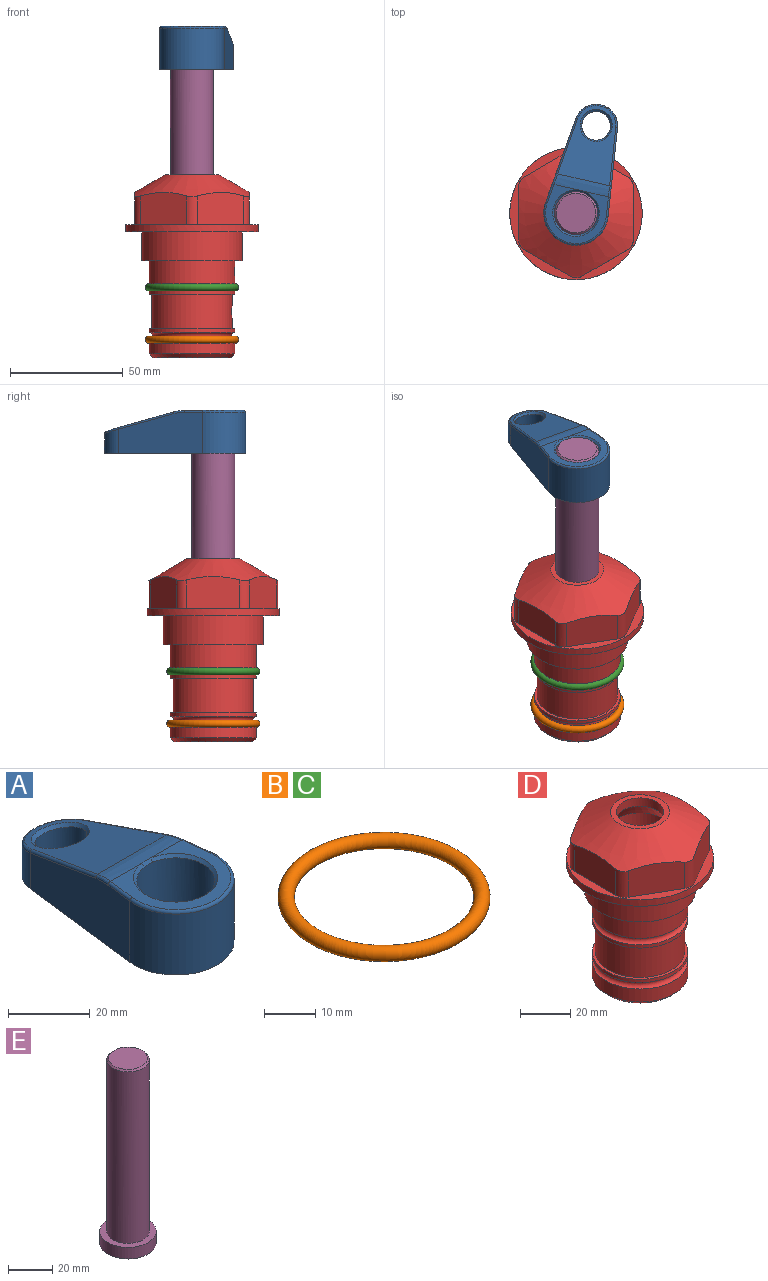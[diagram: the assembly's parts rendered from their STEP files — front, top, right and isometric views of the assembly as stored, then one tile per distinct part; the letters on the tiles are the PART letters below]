
ASSEMBLY  parts=5 mates=4
PART A: 31 faces, bbox 31.7x65.5x19.8 mm
  f0: plane 39.12x18.26mm, normal (0.99,0.12,0), area 612.2mm2, adj f1,f4,f7,f11,f13,f15
  f1: cylinder r=9.53mm len=18.91mm, axis (0,0,-1), area 296.1mm2, adj f0,f2,f7,f17
  f2: plane 39.12x18.26mm, normal (-0.99,0.12,0), area 612.2mm2, adj f1,f4,f7,f12,f14,f16
  f3: cylinder r=6.35mm len=12.7mm, axis (0,0,-1), area 362.4mm2, adj f7,f18
  f4: cylinder r=14.29mm len=28.58mm, axis (0,0,-1), area 882.2mm2, adj f0,f2,f7,f10
  f5: cylinder r=9.53mm len=19.05mm, axis (0,0,-1), area 1092.6mm2, adj f7,f19,f20
  f6: plane 26.99x23.69mm, normal (0,0,1), area 216.2mm2, adj f9,f10,f11,f12,f19
  f7: plane 63.5x28.58mm, normal (0,0,-1), area 661.8mm2, adj f0,f1,f2,f3,f4,f5,f22,f23
  f8: plane 33.52x23.6mm, normal (0,0.26,0.97), area 486mm2, adj f9,f15,f16,f17,f18
  f9: cylinder r=19.05mm len=24.72mm, axis (1,0,0), area 120.4mm2, adj f6,f8,f13,f14,f20
  f10: torus R=13.49mm, axis (0,0,1), area 59mm2, adj f4,f6,f11,f12
  f11: cylinder r=0.79mm len=8.67mm, axis (0.12,-0.99,0), area 10.8mm2, adj f0,f6,f10,f13
  f12: cylinder r=0.79mm len=8.67mm, axis (0.12,0.99,0), area 10.8mm2, adj f2,f6,f10,f14
  f13: bspline ~4.95x1.42mm, area 6.1mm2, adj f0,f9,f11,f15
  f14: bspline ~4.95x1.42mm, area 6.1mm2, adj f2,f9,f12,f16
  f15: cylinder r=0.79mm len=25.95mm, axis (0.12,-0.96,0.26), area 32.9mm2, adj f0,f8,f13,f17
  f16: cylinder r=0.79mm len=25.95mm, axis (0.12,0.96,-0.26), area 32.9mm2, adj f2,f8,f14,f17
  f17: bspline ~18.91x8.38mm, area 30mm2, adj f1,f8,f15,f16
  f18: bspline ~14.29x14.29mm, area 48.3mm2, adj f3,f8
  f19: cone r=9.53mm half-angle=45deg, axis (0,0,1), area 66.5mm2, adj f5,f6,f20
  f20: bspline ~3.22x0.96mm, area 3.5mm2, adj f5,f9,f19
  f21: plane 2.75x2.72mm, normal (0,0,-1), area 2.9mm2, adj f23,f25,f28
  f22: plane 23.05x15.88mm, normal (-0.99,-0.12,0), area 323.6mm2, adj f7,f25,f26,f27,f28,f29
  f23: plane 23.05x15.88mm, normal (0.99,-0.12,0), area 323.6mm2, adj f7,f21,f25,f27,f28,f30
  f24: cylinder r=9.53mm len=10.69mm, axis (0,0,-1), area 114.7mm2, adj f7,f27,f29,f30
  f25: cylinder r=12.7mm len=20.59mm, axis (0,0,-1), area 381.1mm2, adj f7,f21,f22,f23,f26,f28
  f26: plane 2.75x2.72mm, normal (0,0,-1), area 2.9mm2, adj f22,f25,f28
  f27: plane 19.72x18.37mm, normal (0,-0.26,-0.97), area 291.8mm2, adj f22,f23,f24,f28,f29,f30
  f28: cylinder r=15.88mm len=19.92mm, axis (1,0,0), area 54.8mm2, adj f21,f22,f23,f25,f26,f27
  f29: cylinder r=1.59mm len=11mm, axis (0,0,-1), area 34.7mm2, adj f7,f22,f24,f27
  f30: cylinder r=1.59mm len=11mm, axis (0,0,-1), area 34.7mm2, adj f7,f23,f24,f27
PART B: 1 faces, bbox 44.7x44.7x3.2 mm
  f0: torus R=19.05mm, axis (0,0,1), area 1193.9mm2
PART C: same geometry as B
PART D: 36 faces, bbox 58.7x58.7x81 mm
  f0: cylinder r=17.78mm len=35.56mm, axis (0,0,1), area 1670.8mm2, adj f23,f24,f31
  f1: cylinder r=19.05mm len=38.1mm, axis (0,0,1), area 1191.9mm2, adj f26,f27,f30
  f2: plane 58.66x58.66mm, normal (0,0,-1), area 1150.6mm2, adj f3,f28
  f3: cylinder r=29.33mm len=58.66mm, axis (0,0,-1), area 585.1mm2, adj f2,f4
  f4: plane 58.66x58.66mm, normal (0,0,1), area 475.9mm2, adj f3,f5,f6,f7,f8,f9,f10,f11
  f5: plane 20.32x14.34mm, normal (-0.5,0.87,0), area 324.4mm2, adj f4,f15,f16,f17
  f6: plane 20.32x14.34mm, normal (0.5,0.87,0), area 324.4mm2, adj f4,f14,f15,f17
  f7: plane 23.48x14.34mm, normal (1,0,0), area 324.4mm2, adj f4,f13,f14,f17
  f8: plane 20.32x14.34mm, normal (0.5,-0.87,0), area 324.4mm2, adj f4,f12,f13,f17
  f9: plane 20.32x14.34mm, normal (-0.5,-0.87,0), area 324.4mm2, adj f4,f11,f12,f17
  f10: plane 23.48x14.34mm, normal (-1,0,0), area 324.4mm2, adj f4,f11,f16,f17
  f11: cylinder r=5.08mm len=12.85mm, axis (0,0,-1), area 67.2mm2, adj f4,f9,f10,f17
  f12: cylinder r=5.08mm len=12.85mm, axis (0,0,-1), area 67.2mm2, adj f4,f8,f9,f17
  f13: cylinder r=5.08mm len=12.85mm, axis (0,0,-1), area 67.2mm2, adj f4,f7,f8,f17
  f14: cylinder r=5.08mm len=12.85mm, axis (0,0,-1), area 67.2mm2, adj f4,f6,f7,f17
  f15: cylinder r=5.08mm len=12.85mm, axis (0,0,-1), area 67.2mm2, adj f4,f5,f6,f17
  f16: cylinder r=5.08mm len=12.85mm, axis (0,0,-1), area 67.2mm2, adj f4,f5,f10,f17
  f17: cone r=11.73mm half-angle=60deg, axis (0,0,-1), area 2071.8mm2, adj f5,f6,f7,f8,f9,f10,f11,f12
  f18: plane 23.46x23.46mm, normal (0,0,1), area 147.4mm2, adj f17,f35
  f19: plane 34.93x34.93mm, normal (0,0,-1), area 958mm2, adj f29
  f20: cylinder r=19.05mm len=38.1mm, axis (0,0,1), area 760.1mm2, adj f21,f29
  f21: torus R=19.05mm, axis (0,0,1), area 565.3mm2, adj f20,f22
  f22: cylinder r=19.05mm len=38.1mm, axis (0,0,1), area 190mm2, adj f21,f23
  f23: plane 38.1x38.1mm, normal (0,0,1), area 146.9mm2, adj f0,f22
  f24: plane 38.1x38.1mm, normal (0,0,-1), area 146.9mm2, adj f0,f25
  f25: cylinder r=19.05mm len=38.1mm, axis (0,0,1), area 190mm2, adj f24,f26
  f26: torus R=19.05mm, axis (0,0,1), area 565.3mm2, adj f1,f25
  f27: plane 44.45x44.45mm, normal (0,0,-1), area 411.7mm2, adj f1,f28
  f28: cylinder r=22.23mm len=44.45mm, axis (0,0,1), area 1773.5mm2, adj f2,f27
  f29: cone r=19.05mm half-angle=45deg, axis (0,0,1), area 257.5mm2, adj f19,f20
  f30: cylinder r=3.17mm len=6.75mm, axis (-1,0,0), area 128mm2, adj f1,f33
  f31: cylinder r=3.17mm len=6.35mm, axis (-1,0,0), area 102.5mm2, adj f0,f33
  f32: plane 25.4x25.4mm, normal (0,0,1), area 506.7mm2, adj f33
  f33: cylinder r=12.7mm len=66.42mm, axis (0,0,-1), area 5236.2mm2, adj f30,f31,f32,f34
  f34: cone r=9.53mm half-angle=30deg, axis (0,0,-1), area 443.4mm2, adj f33,f35
  f35: cylinder r=9.53mm len=19.05mm, axis (0,0,-1), area 240.9mm2, adj f18,f34
PART E: 6 faces, bbox 25.4x25.4x101.6 mm
  f0: plane 17.46x17.46mm, normal (0,0,1), area 239.5mm2, adj f5
  f1: plane 25.4x25.4mm, normal (0,0,-1), area 506.7mm2, adj f2
  f2: cylinder r=12.7mm len=25.4mm, axis (0,0,1), area 506.7mm2, adj f1,f3
  f3: plane 25.4x25.4mm, normal (0,0,1), area 221.7mm2, adj f2,f4
  f4: cylinder r=9.53mm len=94.46mm, axis (0,0,1), area 5653mm2, adj f3,f5
  f5: cone r=8.73mm half-angle=45deg, axis (0,0,-1), area 64.4mm2, adj f0,f4
PLACE A rot(axis=(0,0,-1),13deg) t=(0,0,27.55)mm
PLACE B t=(0,0,-23.18)mm
PLACE C at identity
PLACE D at identity fixed
PLACE E rot(axis=(0,0,-1),13deg) t=(0,0,27.55)mm
MATE cylindrical E.f2 <-> D.f0  axis (0,0,-1) through (0,0,-10.55)mm
MATE fastened B.f0 <-> D.f0  axis (0,0,1) through (0,0,-47.69)mm
MATE fastened E.f2 <-> A.f4  axis (0,0,1) through (0,0,91.05)mm
MATE fastened C.f0 <-> D.f0  axis (0,0,1) through (0,0,-24.51)mm
